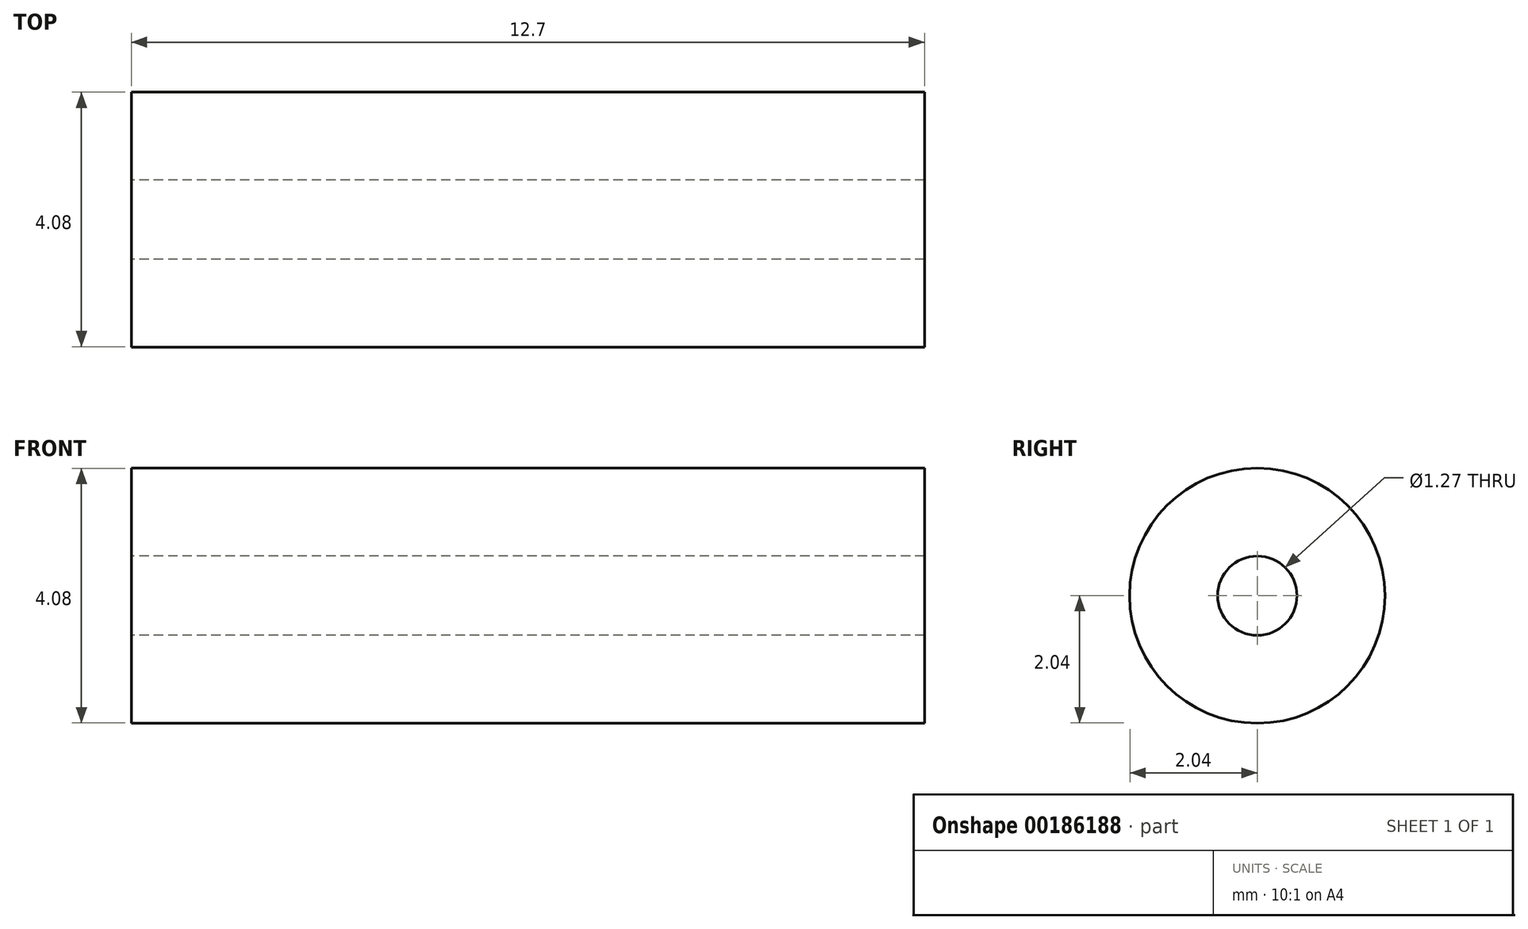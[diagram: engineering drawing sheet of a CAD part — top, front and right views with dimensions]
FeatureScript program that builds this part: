
annotation { "Feature Type Name" : "Feature", "Feature Type Description" : "" }
export const myFeature = defineFeature(function(context is Context, id is Id, definition is map)
    precondition{}
    {
        {
            var Q0;
            Q0=qCreatedBy(makeId("Front.planeOp"),FACE);
            var sketch = newSketch(context, id + "F0", { "sketchPlane" : qUnion([Q0])});
            skLineSegment(sketch, "E0.bottom", {"start": v(0, 0.64) * mm, "end": v(12.7, 0.64) * mm});
            skLineSegment(sketch, "E0.top", {"start": v(0, 2.04) * mm, "end": v(12.7, 2.04) * mm});
            skLineSegment(sketch, "E0.left", {"start": v(0, 0.64) * mm, "end": v(0, 2.04) * mm});
            skLineSegment(sketch, "E0.right", {"start": v(12.7, 0.64) * mm, "end": v(12.7, 2.04) * mm});
            skLineSegment(sketch, "E1", {"start": v(0, 0) * mm, "end": v(12.7, 0) * mm});
            skSolve(sketch);
        }
        {
            var Q0;
            Q0 = qSketchRegion(id + "F0", true);
            var Q1;
            Q1=sQuery(id+"F0.wireOp",EDGE,"E1");
            revolve(context, id + "F1", {"entities" : qUnion([Q0]), "axis" : qUnion([Q1]), "revolveType" : RevolveType.FULL});
        }
    });
